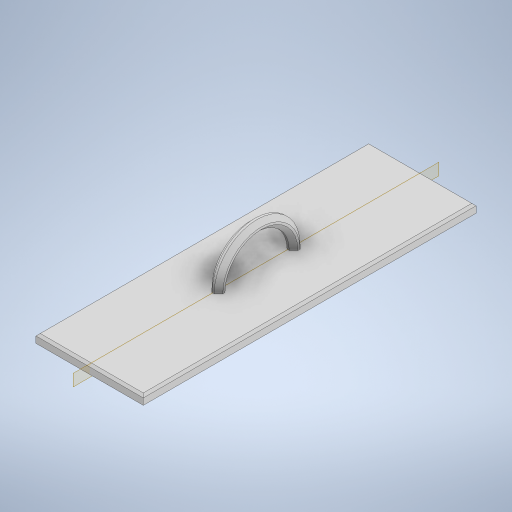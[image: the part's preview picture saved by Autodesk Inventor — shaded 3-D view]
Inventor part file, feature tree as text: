
AUTODESK INVENTOR PART (.ipt)
format: ipt  version: 2023 (Build 270158000, 158)  size: 296,960 bytes
history: native  units: mm
features: extrude x3, chamfer x3, sketch x3, plane x1
ambient origin geometry x8: Origin, YZ Plane, XZ Plane, XY Plane, X Axis, Y Axis, Z Axis, Center Point
bodies: Solid1 (feature_tree)
feature tree (10):
  extrude  "Extrusion1"  Depth=50.0mm
  extrude  "Extrusion2"  Depth=38.0mm
  plane  "Work Plane1"
  extrude  "Extrusion3"  Depth=6.0mm
  chamfer  "Chamfer1"  Distance=6.5mm
  chamfer  "Chamfer2"  Distance=5.0mm
  chamfer  "Chamfer3"  [1 undecoded]
  sketch  "Sketch1"  dims[d0=155.0mm d1=50.0mm]
  sketch  "Sketch2"  dims[d2=5.0mm d3=0.0mm d4=38.0mm]
  sketch  "Sketch3"  dims[d5=142.0mm d6=6.0mm d7=6.5mm d8=5.0mm d9=0.0mm d10=-25.0mm d11=77.5mm d12=0.0mm d13=20.0mm d14=20.0mm d15=20.0mm d16=5.0mm d17=5.0mm d18=5.0mm d19=5.0mm d20=0.0mm d21=2.0mm d22=2.0mm d23=45.0deg d24=1.0mm d25=2.0mm d26=45.0deg d27=1.0mm d28=2.0mm d29=45.0deg]
note: 1 required parameter value undecoded (feature->parameter linkage not recoverable at this tier; creation-order binding heuristic only, values carry confidence <= 0.55)
